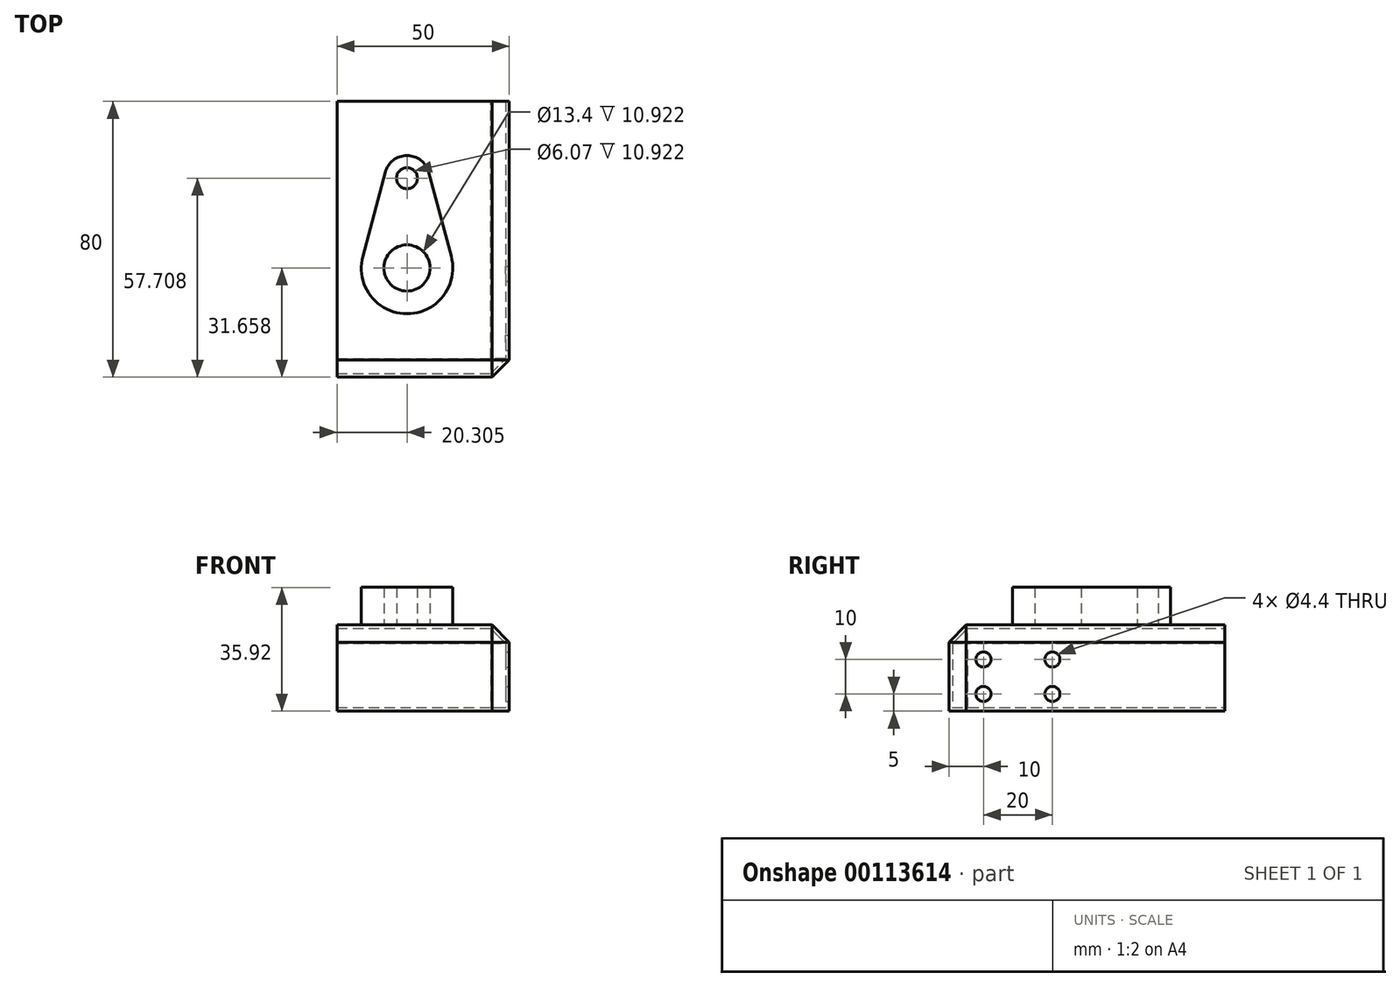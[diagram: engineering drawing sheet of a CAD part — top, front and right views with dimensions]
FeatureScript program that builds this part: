
annotation { "Feature Type Name" : "Feature", "Feature Type Description" : "" }
export const myFeature = defineFeature(function(context is Context, id is Id, definition is map)
    precondition{}
    {
        {
            var Q0;
            Q0=qCreatedBy(makeId("Top.planeOp"),FACE);
            var sketch = newSketch(context, id + "F0", { "sketchPlane" : qUnion([Q0])});
            skLineSegment(sketch, "E0.bottom", {"start": v(0, 0) * mm, "end": v(50, 0) * mm});
            skLineSegment(sketch, "E0.top", {"start": v(0, 80) * mm, "end": v(50, 80) * mm});
            skLineSegment(sketch, "E0.left", {"start": v(0, 0) * mm, "end": v(0, 80) * mm});
            skLineSegment(sketch, "E0.right", {"start": v(50, 0) * mm, "end": v(50, 80) * mm});
            skSolve(sketch);
        }
        {
            var Q0;
            Q0=makeQuery(id+"F0.imprint","IMPRINT",FACE,{"disambiguationData":[TD([[makeQuery(id+"F0.imprint","IMPRINT",EDGE,{"derivedFrom":sQuery(id+"F0.wireOp",EDGE,"E0.bottom")}),1.0]])]});
            extrude(context, id + "F7", {"entities" : qUnion([Q0]), "depth" : 25 * mm});
        }
        {
            var Q0;
            Q0=makeQuery(id+"F7.opExtrude","SWEPT_EDGE",EDGE,{"disambiguationData":[OSD([sQuery(id+"F0.wireOp",EDGE,"E0.bottom"),sQuery(id+"F0.wireOp",EDGE,"E0.right")])]});
            var Q1;
            Q1=makeQuery(id+"F7.opExtrude","CAP_EDGE",EDGE,{"disambiguationData":[OSD([sQuery(id+"F0.wireOp",EDGE,"E0.right")])],"isStart":false});
            var Q2;
            Q2=makeQuery(id+"F7.opExtrude","CAP_EDGE",EDGE,{"disambiguationData":[OSD([sQuery(id+"F0.wireOp",EDGE,"E0.bottom")])],"isStart":false});
            chamfer(context, id + "F1", {"entities" : qUnion([Q0, Q1, Q2]), "width" : 5 * mm, "tangentPropagation" : true});
        }
        {
            var Q0;
            Q0=makeQuery(id+"F7.opExtrude","SWEPT_FACE",FACE,{"disambiguationData":[OSD([sQuery(id+"F0.wireOp",EDGE,"E0.left")])]});
            var Q1;
            Q1=makeQuery(id+"F7.opExtrude","SWEPT_FACE",FACE,{"disambiguationData":[OSD([sQuery(id+"F0.wireOp",EDGE,"E0.top")])]});
            var Q2;
            Q2=makeQuery(id+"F7.opExtrude","SWEPT_BODY",BODY,{"disambiguationData":[OSD([sQuery(id+"F0.wireOp",EDGE,"E0.bottom"),sQuery(id+"F0.wireOp",EDGE,"E0.top"),sQuery(id+"F0.wireOp",EDGE,"E0.left"),sQuery(id+"F0.wireOp",EDGE,"E0.right")])]});
            shell(context, id + "F2", {"entities" : qUnion([Q0, Q1]), "parts" : qUnion([Q2]), "thickness" : 1 * mm});
        }
        {
            var Q0;
            Q0=makeQuery(id+"F7.opExtrude","CAP_FACE",FACE,{"disambiguationData":[OSD([sQuery(id+"F0.wireOp",EDGE,"E0.bottom"),sQuery(id+"F0.wireOp",EDGE,"E0.top"),sQuery(id+"F0.wireOp",EDGE,"E0.left"),sQuery(id+"F0.wireOp",EDGE,"E0.right")])],"isStart":false});
            var sketch = newSketch(context, id + "F3", { "sketchPlane" : qUnion([Q0])});
            skArc(sketch, "E1", {"start": v(26.64, 59.4) * mm, "mid": v(20.3, 64.27) * mm, "end": v(13.97, 59.4) * mm});
            skArc(sketch, "E2", {"start": v(7.47, 35.08) * mm, "mid": v(20.3, 18.38) * mm, "end": v(33.14, 35.08) * mm});
            skLineSegment(sketch, "E3", {"start": v(13.97, 59.4) * mm, "end": v(7.47, 35.08) * mm});
            skLineSegment(sketch, "E4", {"start": v(26.64, 59.4) * mm, "end": v(33.14, 35.08) * mm});
            skCircle(sketch, "E5", {"center": v(20.3, 31.66) * mm, "radius": 6.7 * mm});
            skCircle(sketch, "E6", {"center": v(20.3, 57.7) * mm, "radius": 3.03 * mm});
            skSolve(sketch);
        }
        {
            var Q0;
            Q0=makeQuery(id+"F3.imprint","IMPRINT",FACE,{"disambiguationData":[TD([[makeQuery(id+"F3.imprint","IMPRINT",EDGE,{"derivedFrom":sQuery(id+"F3.wireOp",EDGE,"E1")}),1.0]])]});
            extrude(context, id + "F4", {"entities" : qUnion([Q0]), "operationType" : NewBodyOperationType.ADD, "depth" : 10.92 * mm});
        }
        {
            var Q0;
            Q0=makeQuery(id+"F7.opExtrude","SWEPT_FACE",FACE,{"disambiguationData":[OSD([sQuery(id+"F0.wireOp",EDGE,"E0.right")])]});
            var sketch = newSketch(context, id + "F5", { "sketchPlane" : qUnion([Q0])});
            skPoint(sketch, "E7", {"position": v(10, 15) * mm});
            skPoint(sketch, "E8", {"position": v(10, 5) * mm});
            skPoint(sketch, "E9", {"position": v(30, 5) * mm});
            skPoint(sketch, "E10", {"position": v(30, 15) * mm});
            skSolve(sketch);
        }
        {
            var Q0;
            Q0=sQuery(id+"F5.wireOp",VERTEX,"E7");
            var Q1;
            Q1=sQuery(id+"F5.wireOp",VERTEX,"E10");
            var Q2;
            Q2=sQuery(id+"F5.wireOp",VERTEX,"E9");
            var Q3;
            Q3=sQuery(id+"F5.wireOp",VERTEX,"E8");
            var Q4;
            Q4=makeQuery(id+"F7.opExtrude","SWEPT_BODY",BODY,{"disambiguationData":[OSD([sQuery(id+"F0.wireOp",EDGE,"E0.bottom"),sQuery(id+"F0.wireOp",EDGE,"E0.top"),sQuery(id+"F0.wireOp",EDGE,"E0.left"),sQuery(id+"F0.wireOp",EDGE,"E0.right")])]});
            hole(context, id + "F6", {"style" : HoleStyle.SIMPLE, "endStyle" : HoleEndStyle.THROUGH, "standardTappedOrClearance" : lookupTablePath({ "standard" : "ISO", "fit" : "Normal", "size" : "M4", "type" : "Clearance" }), "standardBlindInLast" : lookupTablePath({ "fit" : "Standard", "standard" : "ISO", "size" : "M4", "type" : "Clearance" }), "holeDiameter" : 4.4 * mm, "locations" : qUnion([Q0, Q1, Q2, Q3]), "scope" : qUnion([Q4]), "isTappedThrough" : true});
        }
    });
